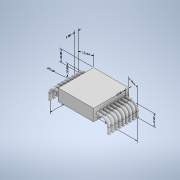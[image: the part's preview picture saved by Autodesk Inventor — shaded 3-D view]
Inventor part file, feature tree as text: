
AUTODESK INVENTOR PART (.ipt)
format: ipt  version: 2021 (Build 250183000, 183)  size: 322,048 bytes
history: native  units: mm
features: other x12, sketch x5, sweep x2, extrude x1
ambient origin geometry x8: Origin, YZ Plane, XZ Plane, XY Plane, X Axis, Y Axis, Z Axis, Center Point
bodies: Body1 (feature_tree)
feature tree (20):
  other  "Твердое тело1"
  other  "Аннотации"
  extrude  "Выдавливание1"  Depth=30.0mm
  sweep  "Сдвиг1"
  sweep  "Сдвиг2"
  sketch  "Эскиз1"
  sketch  "Эскиз2"
  sketch  "3D эскиз1"
  sketch  "Эскиз3"
  sketch  "3D эскиз2"
  other  "Линейный размер 1"
  other  "Линейный размер 2"
  other  "Линейный размер 3"
  other  "Линейный размер 4"
  other  "Линейный размер 5"
  other  "Линейный размер 6"
  other  "Линейный размер 7"
  other  "Линейный размер 8"
  other  "Диаметр 1"
  other  "Линейный размер 9"
